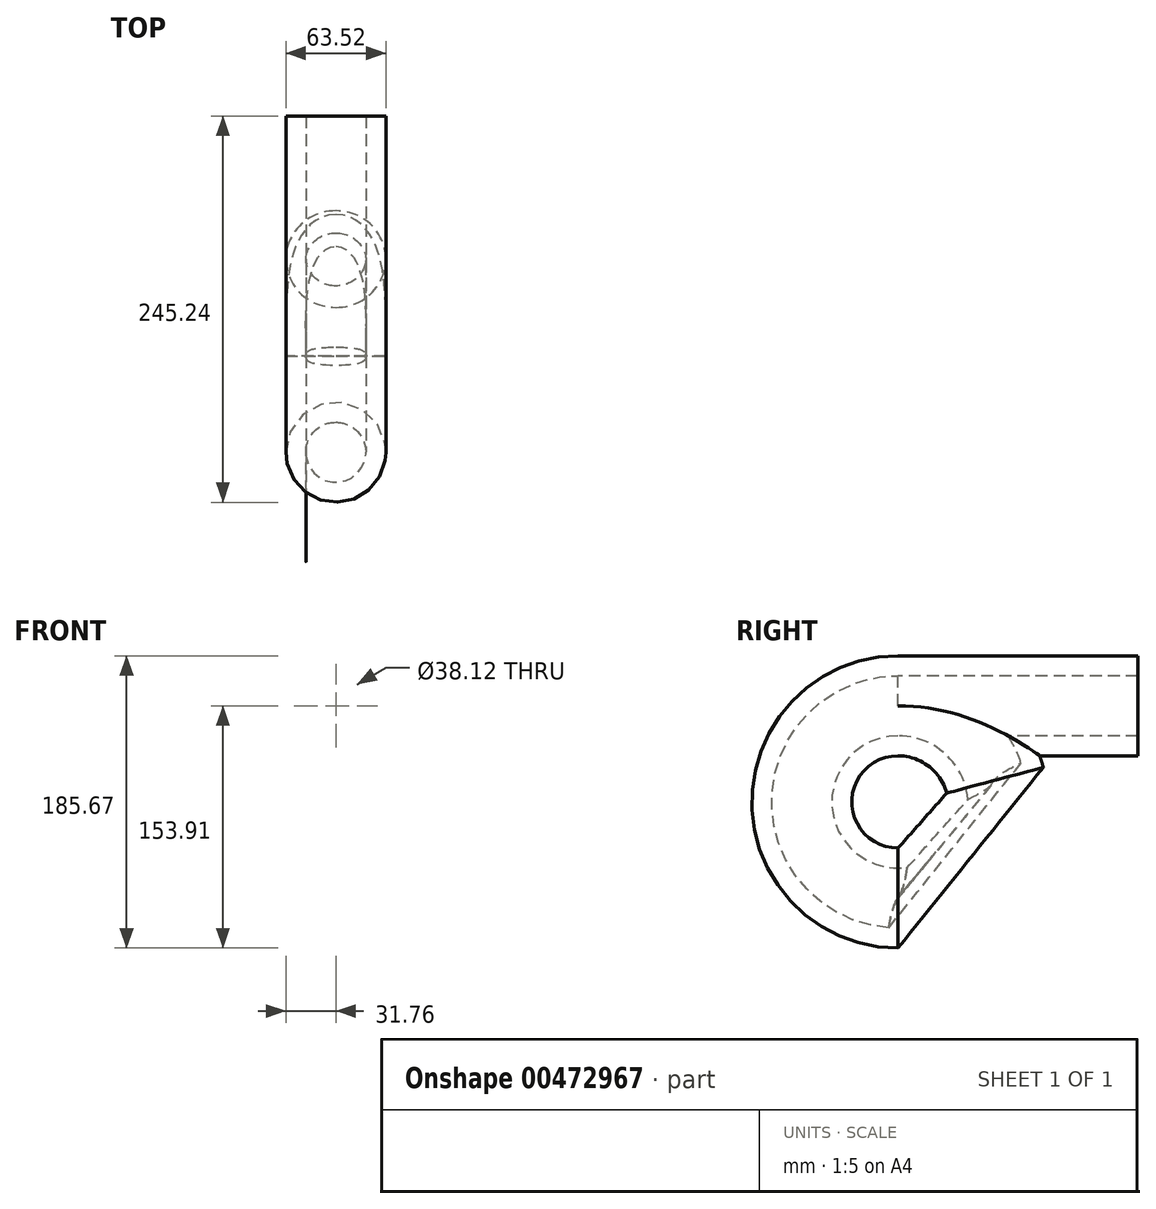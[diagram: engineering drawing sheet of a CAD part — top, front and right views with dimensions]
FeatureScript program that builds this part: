
annotation { "Feature Type Name" : "Feature", "Feature Type Description" : "" }
export const myFeature = defineFeature(function(context is Context, id is Id, definition is map)
    precondition{}
    {
        {
            var Q0;
            Q0=qCreatedBy(makeId("Front.planeOp"),FACE);
            var sketch = newSketch(context, id + "F0", { "sketchPlane" : qUnion([Q0])});
            skCircle(sketch, "E0", {"center": v(0, 0) * mm, "radius": 31.76 * mm});
            skLineSegment(sketch, "E1", {"start": v(0, -63.81) * mm, "end": v(54.31, -63.81) * mm});
            skSolve(sketch);
        }
        {
            var Q0;
            Q0=qCreatedBy(makeId("Right.planeOp"),FACE);
            var sketch = newSketch(context, id + "F1", { "sketchPlane" : qUnion([Q0])});
            skArc(sketch, "E2", {"start": v(0, -10.25) * mm, "mid": v(-50.83, -61.08) * mm, "end": v(0, -111.9) * mm});
            skSolve(sketch);
        }
        {
            var Q0;
            Q0=makeQuery(id+"F0.imprint","IMPRINT",FACE,{"disambiguationData":[TD([[makeQuery(id+"F0.imprint","IMPRINT",EDGE,{"derivedFrom":sQuery(id+"F0.wireOp",EDGE,"E0")}),1.0]])]});
            extrude(context, id + "F2", {"entities" : qUnion([Q0]), "oppositeDirection" : true, "depth" : 152.4 * mm});
        }
        {
            var Q0;
            Q0=makeQuery(id+"F0.imprint","IMPRINT",FACE,{"disambiguationData":[TD([[makeQuery(id+"F0.imprint","IMPRINT",EDGE,{"derivedFrom":sQuery(id+"F0.wireOp",EDGE,"E0")}),1.0]])]});
            var Q1;
            Q1=sQuery(id+"F0.wireOp",EDGE,"E0");
            var Q2;
            Q2=sQuery(id+"F0.wireOp",EDGE,"E1");
            revolve(context, id + "F3", {"operationType" : NewBodyOperationType.ADD, "entities" : qUnion([Q0]), "surfaceEntities" : qUnion([Q1]), "axis" : qUnion([Q2]), "revolveType" : RevolveType.ONE_DIRECTION, "oppositeDirection" : true, "angle" : 75 * degree});
        }
        {
            var Q0;
            Q0=makeQuery(id+"F0.imprint","IMPRINT",FACE,{"disambiguationData":[TD([[makeQuery(id+"F0.imprint","IMPRINT",EDGE,{"derivedFrom":sQuery(id+"F0.wireOp",EDGE,"E0")}),1.0]])]});
            var Q1;
            Q1=sQuery(id+"F1.wireOp",EDGE,"E2");
            sweep(context, id + "F4", {"profiles" : qUnion([Q0]), "path" : qUnion([Q1])});
        }
        {
            var Q1;
            Q1=makeQuery(id+"F3.opRevolve","CAP_FACE",FACE,{"disambiguationData":[OSD([sQuery(id+"F0.wireOp",EDGE,"E0")])],"isStart":false});
            var Q2;
            Q2=makeQuery(id+"F4.opSweep","CAP_FACE",FACE,{"disambiguationData":[OSD([sQuery(id+"F0.wireOp",EDGE,"E0"),sQuery(id+"F1.wireOp",VERTEX,"E2.end")])],"isStart":false});
            loft(context, id + "F5", {"operationType" : NewBodyOperationType.ADD, "sheetProfilesArray" : [{ "sheetProfileEntities" : qUnion([Q1]) }, { "sheetProfileEntities" : qUnion([Q2]) }]});
        }
        {
            var Q0;
            Q0=makeQuery(id+"F2.opExtrude","CAP_FACE",FACE,{"disambiguationData":[OSD([sQuery(id+"F0.wireOp",EDGE,"E0")])],"isStart":false});
            shell(context, id + "F6", {"entities" : qUnion([Q0]), "thickness" : 12.7 * mm});
        }
    });
